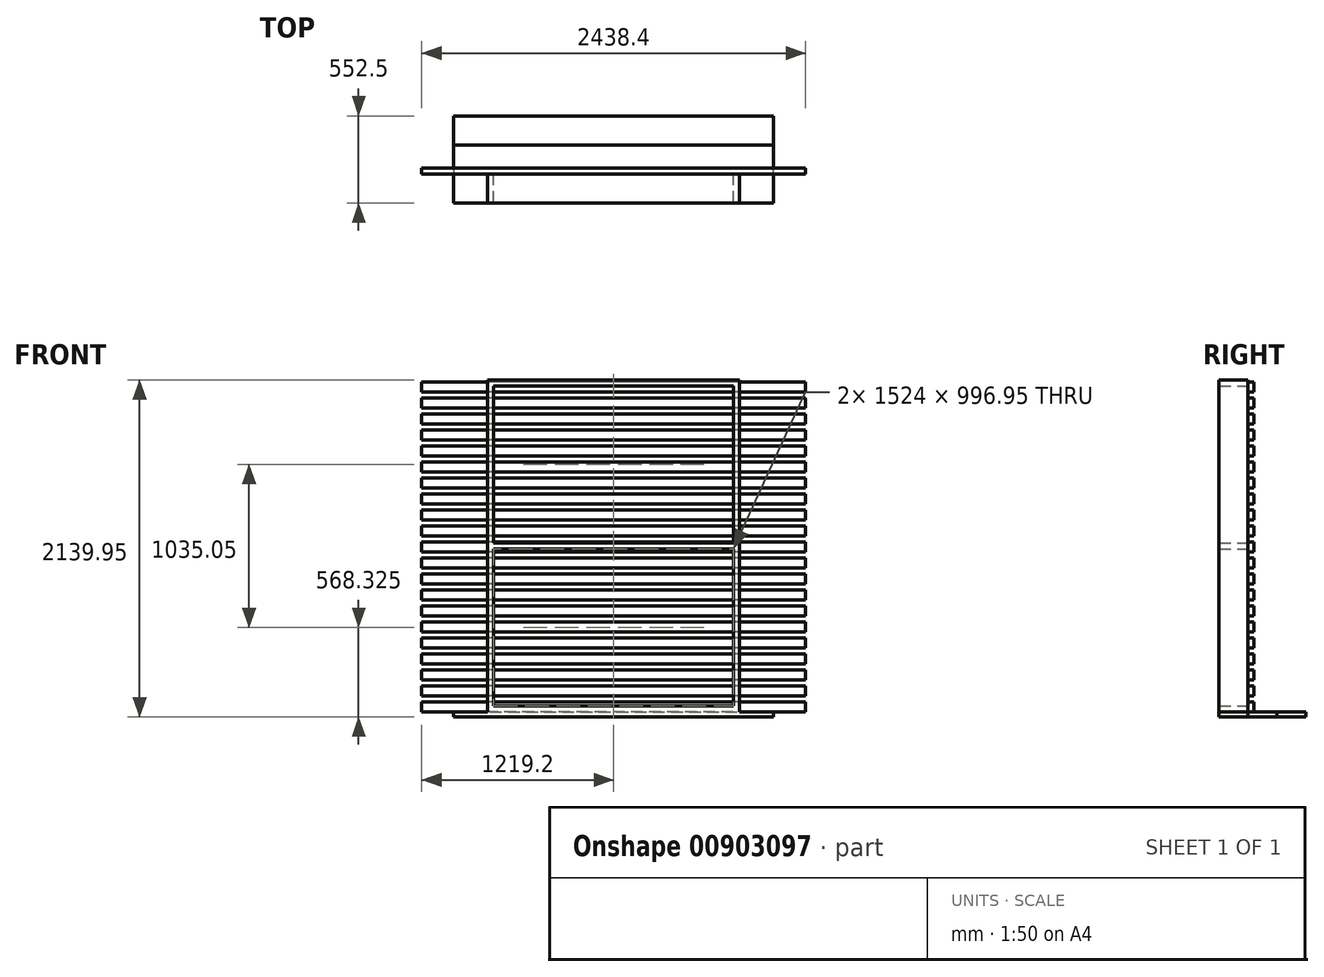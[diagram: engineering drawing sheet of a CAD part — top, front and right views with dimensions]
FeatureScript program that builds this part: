
annotation { "Feature Type Name" : "Feature", "Feature Type Description" : "" }
export const myFeature = defineFeature(function(context is Context, id is Id, definition is map)
    precondition{}
    {
        {
            var Q0;
            Q0=qCreatedBy(makeId("Front.planeOp"),FACE);
            var sketch = newSketch(context, id + "F0", { "sketchPlane" : qUnion([Q0])});
            skLineSegment(sketch, "E0.bottom", {"start": v(762, 1016) * mm, "end": v(-762, 1016) * mm});
            skLineSegment(sketch, "E0.top", {"start": v(762, -1016) * mm, "end": v(-762, -1016) * mm});
            skLineSegment(sketch, "E0.left", {"start": v(762, 1016) * mm, "end": v(762, -1016) * mm});
            skLineSegment(sketch, "E0.right", {"start": v(-762, 1016) * mm, "end": v(-762, -1016) * mm});
            skPoint(sketch, "E0.middle", {"position": v(0, 0) * mm});
            skLineSegment(sketch, "E1.0", {"start": v(800.1, 1054.1) * mm, "end": v(-800.1, 1054.1) * mm});
            skLineSegment(sketch, "E1.1", {"start": v(800.1, 1054.1) * mm, "end": v(800.1, -1054.1) * mm});
            skLineSegment(sketch, "E1.2", {"start": v(800.1, -1054.1) * mm, "end": v(-800.1, -1054.1) * mm});
            skLineSegment(sketch, "E1.3", {"start": v(-800.1, 1054.1) * mm, "end": v(-800.1, -1054.1) * mm});
            skSolve(sketch);
        }
        {
            var Q0;
            Q0=makeQuery(id+"F0.imprint","IMPRINT",FACE,{"disambiguationData":[TD([[makeQuery(id+"F0.imprint","IMPRINT",EDGE,{"derivedFrom":sQuery(id+"F0.wireOp",EDGE,"E0.bottom")}),-1.0]])]});
            extrude(context, id + "F1", {"entities" : qUnion([Q0]), "depth" : 184.15 * mm, "offsetDistance" : 25.4 * mm});
        }
        {
            var Q0;
            Q0=makeQuery(id+"F1.opExtrude","CAP_FACE",FACE,{"disambiguationData":[OSD([sQuery(id+"F0.wireOp",EDGE,"E0.bottom"),sQuery(id+"F0.wireOp",EDGE,"E0.top"),sQuery(id+"F0.wireOp",EDGE,"E0.left"),sQuery(id+"F0.wireOp",EDGE,"E0.right"),sQuery(id+"F0.wireOp",EDGE,"E1.0"),sQuery(id+"F0.wireOp",EDGE,"E1.1"),sQuery(id+"F0.wireOp",EDGE,"E1.2"),sQuery(id+"F0.wireOp",EDGE,"E1.3")])],"isStart":true});
            var sketch = newSketch(context, id + "F2", { "sketchPlane" : qUnion([Q0])});
            skLineSegment(sketch, "E2.bottom", {"start": v(952.5, -92.07) * mm, "end": v(-952.5, -92.08) * mm});
            skLineSegment(sketch, "E2.top", {"start": v(952.5, 92.08) * mm, "end": v(-952.5, 92.07) * mm});
            skLineSegment(sketch, "E2.left", {"start": v(952.5, -92.07) * mm, "end": v(952.5, 92.08) * mm});
            skLineSegment(sketch, "E2.right", {"start": v(-952.5, -92.08) * mm, "end": v(-952.5, 92.07) * mm});
            skPoint(sketch, "E2.middle", {"position": v(0, 0) * mm});
            skLineSegment(sketch, "E3.0.1.0", {"start": v(953.01, 111.12) * mm, "end": v(-951.99, 111.12) * mm});
            skPoint(sketch, "E3.0.1.1", {"position": v(0.51, 203.2) * mm});
            skLineSegment(sketch, "E3.0.1.2", {"start": v(953.01, 111.12) * mm, "end": v(953.01, 295.27) * mm});
            skLineSegment(sketch, "E3.0.1.3", {"start": v(953.01, 295.27) * mm, "end": v(-951.99, 295.27) * mm});
            skLineSegment(sketch, "E3.0.1.4", {"start": v(-951.99, 111.12) * mm, "end": v(-951.99, 295.27) * mm});
            skLineSegment(sketch, "E3.0.2.0", {"start": v(953.53, 314.32) * mm, "end": v(-951.47, 314.32) * mm});
            skPoint(sketch, "E3.0.2.1", {"position": v(1.03, 406.4) * mm});
            skLineSegment(sketch, "E3.0.2.2", {"start": v(953.53, 314.32) * mm, "end": v(953.53, 498.47) * mm});
            skLineSegment(sketch, "E3.0.2.3", {"start": v(953.53, 498.47) * mm, "end": v(-951.47, 498.47) * mm});
            skLineSegment(sketch, "E3.0.2.4", {"start": v(-951.47, 314.32) * mm, "end": v(-951.47, 498.47) * mm});
            skLineSegment(sketch, "E3.0.3.0", {"start": v(954.04, 517.52) * mm, "end": v(-950.96, 517.52) * mm});
            skPoint(sketch, "E3.0.3.1", {"position": v(1.54, 609.6) * mm});
            skLineSegment(sketch, "E3.0.3.2", {"start": v(954.04, 517.52) * mm, "end": v(954.04, 701.67) * mm});
            skLineSegment(sketch, "E3.0.3.3", {"start": v(954.04, 701.67) * mm, "end": v(-950.96, 701.67) * mm});
            skLineSegment(sketch, "E3.0.3.4", {"start": v(-950.96, 517.52) * mm, "end": v(-950.96, 701.67) * mm});
            skLineSegment(sketch, "E3.0.4.0", {"start": v(954.56, 720.72) * mm, "end": v(-950.44, 720.72) * mm});
            skPoint(sketch, "E3.0.4.1", {"position": v(2.06, 812.8) * mm});
            skLineSegment(sketch, "E3.0.4.2", {"start": v(954.56, 720.72) * mm, "end": v(954.56, 904.87) * mm});
            skLineSegment(sketch, "E3.0.4.3", {"start": v(954.56, 904.87) * mm, "end": v(-950.44, 904.87) * mm});
            skLineSegment(sketch, "E3.0.4.4", {"start": v(-950.44, 720.72) * mm, "end": v(-950.44, 904.87) * mm});
            skLineSegment(sketch, "E3.0.5.0", {"start": v(955.07, 923.92) * mm, "end": v(-949.93, 923.92) * mm});
            skPoint(sketch, "E3.0.5.1", {"position": v(2.57, 1016) * mm});
            skLineSegment(sketch, "E3.0.5.2", {"start": v(955.07, 923.92) * mm, "end": v(955.07, 1108.07) * mm});
            skLineSegment(sketch, "E3.0.5.3", {"start": v(955.07, 1108.07) * mm, "end": v(-949.93, 1108.07) * mm});
            skLineSegment(sketch, "E3.0.5.4", {"start": v(-949.93, 923.92) * mm, "end": v(-949.93, 1108.07) * mm});
            skLineSegment(sketch, "E3.direction1", {"start": v(-952.5, -92.08) * mm, "end": v(-952.5, -92.08) * mm});
            skLineSegment(sketch, "E3.direction2", {"start": v(-952.5, -92.08) * mm, "end": v(-951.99, 111.12) * mm, "construction": true});
            skLineSegment(sketch, "E4", {"start": v(0, 0) * mm, "end": v(1562.61, 0) * mm});
            skLineSegment(sketch, "E5.MirrorCS", {"start": v(954.56, -720.72) * mm, "end": v(-950.44, -720.72) * mm});
            skPoint(sketch, "E6.MirrorP", {"position": v(1.03, -406.4) * mm});
            skLineSegment(sketch, "E7.MirrorCS", {"start": v(953.01, -111.12) * mm, "end": v(-951.99, -111.12) * mm});
            skLineSegment(sketch, "E8.MirrorCS", {"start": v(-949.93, -923.92) * mm, "end": v(-949.93, -1108.07) * mm});
            skLineSegment(sketch, "E9.MirrorCS", {"start": v(954.04, -517.52) * mm, "end": v(-950.96, -517.52) * mm});
            skLineSegment(sketch, "E10.MirrorCS", {"start": v(953.53, -314.32) * mm, "end": v(953.53, -498.47) * mm});
            skLineSegment(sketch, "E11.MirrorCS", {"start": v(953.01, -111.12) * mm, "end": v(953.01, -295.27) * mm});
            skPoint(sketch, "E12.MirrorP", {"position": v(2.06, -812.8) * mm});
            skLineSegment(sketch, "E13.MirrorCS", {"start": v(-950.96, -517.52) * mm, "end": v(-950.96, -701.67) * mm});
            skLineSegment(sketch, "E14.MirrorCS", {"start": v(953.53, -498.47) * mm, "end": v(-951.47, -498.47) * mm});
            skLineSegment(sketch, "E15.MirrorCS", {"start": v(954.04, -517.52) * mm, "end": v(954.04, -701.67) * mm});
            skLineSegment(sketch, "E16.MirrorCS", {"start": v(955.07, -923.92) * mm, "end": v(-949.93, -923.92) * mm});
            skLineSegment(sketch, "E17.MirrorCS", {"start": v(954.56, -720.72) * mm, "end": v(954.56, -904.87) * mm});
            skLineSegment(sketch, "E18.MirrorCS", {"start": v(955.07, -923.92) * mm, "end": v(955.07, -1108.07) * mm});
            skPoint(sketch, "E19.MirrorP", {"position": v(1.54, -609.6) * mm});
            skLineSegment(sketch, "E20.MirrorCS", {"start": v(-951.99, -111.12) * mm, "end": v(-951.99, -295.27) * mm});
            skLineSegment(sketch, "E21.MirrorCS", {"start": v(954.04, -701.67) * mm, "end": v(-950.96, -701.67) * mm});
            skPoint(sketch, "E22.MirrorP", {"position": v(0.51, -203.2) * mm});
            skLineSegment(sketch, "E23.MirrorCS", {"start": v(953.53, -314.32) * mm, "end": v(-951.47, -314.32) * mm});
            skLineSegment(sketch, "E24.MirrorCS", {"start": v(955.07, -1108.07) * mm, "end": v(-949.93, -1108.07) * mm});
            skLineSegment(sketch, "E25.MirrorCS", {"start": v(953.01, -295.27) * mm, "end": v(-951.99, -295.27) * mm});
            skLineSegment(sketch, "E26.MirrorCS", {"start": v(-951.47, -314.32) * mm, "end": v(-951.47, -498.47) * mm});
            skPoint(sketch, "E27.MirrorP", {"position": v(2.57, -1016) * mm});
            skLineSegment(sketch, "E28.MirrorCS", {"start": v(-950.44, -720.72) * mm, "end": v(-950.44, -904.87) * mm});
            skLineSegment(sketch, "E29.MirrorCS", {"start": v(954.56, -904.87) * mm, "end": v(-950.44, -904.87) * mm});
            skSolve(sketch);
        }
        {
            var Q0;
            Q0=qCreatedBy(makeId("Top.planeOp"),FACE);
            var sketch = newSketch(context, id + "F3", { "sketchPlane" : qUnion([Q0])});
            skLineSegment(sketch, "E30.0", {"start": v(-762, -184.15) * mm, "end": v(-762, 0) * mm});
            skLineSegment(sketch, "E31.0", {"start": v(762, -184.15) * mm, "end": v(762, 0) * mm});
            skLineSegment(sketch, "E32", {"start": v(-762, 0) * mm, "end": v(762, 0) * mm});
            skLineSegment(sketch, "E33", {"start": v(-762, -184.15) * mm, "end": v(762, -184.15) * mm});
            skSolve(sketch);
        }
        {
            var Q0;
            Q0 = qSketchRegion(id + "F3", true);
            extrude(context, id + "F4", {"entities" : qUnion([Q0]), "operationType" : NewBodyOperationType.ADD, "endBound" : BoundingType.SYMMETRIC, "depth" : 38.1 * mm, "offsetDistance" : 25.4 * mm});
        }
        {
            var Q0;
            Q0=makeQuery(id+"F1.opExtrude","SWEPT_FACE",FACE,{"disambiguationData":[OSD([sQuery(id+"F0.wireOp",EDGE,"E1.2")])]});
            var sketch = newSketch(context, id + "F5", { "sketchPlane" : qUnion([Q0])});
            skLineSegment(sketch, "E34", {"start": v(0, 0) * mm, "end": v(-1016, 0) * mm});
            skLineSegment(sketch, "E35", {"start": v(0, 0) * mm, "end": v(1016, 0) * mm});
            skLineSegment(sketch, "E36", {"start": v(-1016, 0) * mm, "end": v(-1016, 184.15) * mm});
            skLineSegment(sketch, "E37", {"start": v(-1016, 184.15) * mm, "end": v(1016, 184.15) * mm});
            skLineSegment(sketch, "E38", {"start": v(1016, 184.15) * mm, "end": v(1016, 0) * mm});
            skLineSegment(sketch, "E39.0.1.0", {"start": v(-1016, -0.03) * mm, "end": v(1016, -0.03) * mm});
            skLineSegment(sketch, "E39.0.1.1", {"start": v(1016, -0.03) * mm, "end": v(1016, -184.18) * mm});
            skLineSegment(sketch, "E39.0.1.2", {"start": v(0, -184.18) * mm, "end": v(1016, -184.18) * mm});
            skLineSegment(sketch, "E39.0.1.3", {"start": v(-1016, -184.18) * mm, "end": v(-1016, -0.03) * mm});
            skLineSegment(sketch, "E39.0.1.4", {"start": v(0, -184.18) * mm, "end": v(-1016, -184.18) * mm});
            skLineSegment(sketch, "E39.0.2.0", {"start": v(-1016, -184.2) * mm, "end": v(1016, -184.2) * mm});
            skLineSegment(sketch, "E39.0.2.1", {"start": v(1016, -184.2) * mm, "end": v(1016, -368.35) * mm});
            skLineSegment(sketch, "E39.0.2.2", {"start": v(0, -368.35) * mm, "end": v(1016, -368.35) * mm});
            skLineSegment(sketch, "E39.0.2.3", {"start": v(-1016, -368.35) * mm, "end": v(-1016, -184.2) * mm});
            skLineSegment(sketch, "E39.0.2.4", {"start": v(0, -368.35) * mm, "end": v(-1016, -368.35) * mm});
            skLineSegment(sketch, "E39.1.1.0", {"start": v(-1016, -0.03) * mm, "end": v(1016, -0.03) * mm});
            skLineSegment(sketch, "E39.1.1.1", {"start": v(1016, -0.03) * mm, "end": v(1016, -184.18) * mm});
            skLineSegment(sketch, "E39.1.1.2", {"start": v(0, -184.18) * mm, "end": v(1016, -184.18) * mm});
            skLineSegment(sketch, "E39.1.1.3", {"start": v(-1016, -184.18) * mm, "end": v(-1016, -0.03) * mm});
            skLineSegment(sketch, "E39.1.1.4", {"start": v(0, -184.18) * mm, "end": v(-1016, -184.18) * mm});
            skLineSegment(sketch, "E39.1.2.0", {"start": v(-1016, -184.2) * mm, "end": v(1016, -184.2) * mm});
            skLineSegment(sketch, "E39.1.2.1", {"start": v(1016, -184.2) * mm, "end": v(1016, -368.35) * mm});
            skLineSegment(sketch, "E39.1.2.2", {"start": v(0, -368.35) * mm, "end": v(1016, -368.35) * mm});
            skLineSegment(sketch, "E39.1.2.3", {"start": v(-1016, -368.35) * mm, "end": v(-1016, -184.2) * mm});
            skLineSegment(sketch, "E39.1.2.4", {"start": v(0, -368.35) * mm, "end": v(-1016, -368.35) * mm});
            skLineSegment(sketch, "E39.2.1.0", {"start": v(-1016, -0.03) * mm, "end": v(1016, -0.03) * mm});
            skLineSegment(sketch, "E39.2.1.1", {"start": v(1016, -0.03) * mm, "end": v(1016, -184.18) * mm});
            skLineSegment(sketch, "E39.2.1.2", {"start": v(0, -184.18) * mm, "end": v(1016, -184.18) * mm});
            skLineSegment(sketch, "E39.2.1.3", {"start": v(-1016, -184.18) * mm, "end": v(-1016, -0.03) * mm});
            skLineSegment(sketch, "E39.2.1.4", {"start": v(0, -184.18) * mm, "end": v(-1016, -184.18) * mm});
            skLineSegment(sketch, "E39.2.2.0", {"start": v(-1016, -184.2) * mm, "end": v(1016, -184.2) * mm});
            skLineSegment(sketch, "E39.2.2.1", {"start": v(1016, -184.2) * mm, "end": v(1016, -368.35) * mm});
            skLineSegment(sketch, "E39.2.2.2", {"start": v(0, -368.35) * mm, "end": v(1016, -368.35) * mm});
            skLineSegment(sketch, "E39.2.2.3", {"start": v(-1016, -368.35) * mm, "end": v(-1016, -184.2) * mm});
            skLineSegment(sketch, "E39.2.2.4", {"start": v(0, -368.35) * mm, "end": v(-1016, -368.35) * mm});
            skLineSegment(sketch, "E39.direction1", {"start": v(-1016, 0) * mm, "end": v(-1016, 0) * mm});
            skLineSegment(sketch, "E39.direction2", {"start": v(-1016, 0) * mm, "end": v(-1016, -184.18) * mm, "construction": true});
            skSolve(sketch);
        }
        {
            var Q0;
            Q0 = qSketchRegion(id + "F5", true);
            extrude(context, id + "F6", {"entities" : qUnion([Q0]), "operationType" : NewBodyOperationType.ADD, "depth" : 31.75 * mm, "offsetDistance" : 25.4 * mm});
        }
        {
            var Q0;
            Q0=qCreatedBy(makeId("Right.planeOp"),FACE);
            var sketch = newSketch(context, id + "F7", { "sketchPlane" : qUnion([Q0])});
            skLineSegment(sketch, "E40.bottom", {"start": v(0, -1054.1) * mm, "end": v(38.1, -1054.1) * mm});
            skLineSegment(sketch, "E40.top", {"start": v(0, -990.6) * mm, "end": v(38.1, -990.6) * mm});
            skLineSegment(sketch, "E40.left", {"start": v(0, -1054.1) * mm, "end": v(0, -990.6) * mm});
            skLineSegment(sketch, "E40.right", {"start": v(38.1, -1054.1) * mm, "end": v(38.1, -990.6) * mm});
            skLineSegment(sketch, "E41.0.1.0", {"start": v(0, -952.5) * mm, "end": v(0, -889) * mm});
            skLineSegment(sketch, "E41.0.1.1", {"start": v(38.1, -952.5) * mm, "end": v(38.1, -889) * mm});
            skLineSegment(sketch, "E41.0.1.2", {"start": v(0, -952.5) * mm, "end": v(38.1, -952.5) * mm});
            skLineSegment(sketch, "E41.0.1.3", {"start": v(0, -889) * mm, "end": v(38.1, -889) * mm});
            skLineSegment(sketch, "E41.0.2.0", {"start": v(0, -850.9) * mm, "end": v(0, -787.4) * mm});
            skLineSegment(sketch, "E41.0.2.1", {"start": v(38.1, -850.9) * mm, "end": v(38.1, -787.4) * mm});
            skLineSegment(sketch, "E41.0.2.2", {"start": v(0, -850.9) * mm, "end": v(38.1, -850.9) * mm});
            skLineSegment(sketch, "E41.0.2.3", {"start": v(0, -787.4) * mm, "end": v(38.1, -787.4) * mm});
            skLineSegment(sketch, "E41.0.3.0", {"start": v(0, -749.3) * mm, "end": v(0, -685.8) * mm});
            skLineSegment(sketch, "E41.0.3.1", {"start": v(38.1, -749.3) * mm, "end": v(38.1, -685.8) * mm});
            skLineSegment(sketch, "E41.0.3.2", {"start": v(0, -749.3) * mm, "end": v(38.1, -749.3) * mm});
            skLineSegment(sketch, "E41.0.3.3", {"start": v(0, -685.8) * mm, "end": v(38.1, -685.8) * mm});
            skLineSegment(sketch, "E41.0.4.0", {"start": v(0, -647.7) * mm, "end": v(0, -584.2) * mm});
            skLineSegment(sketch, "E41.0.4.1", {"start": v(38.1, -647.7) * mm, "end": v(38.1, -584.2) * mm});
            skLineSegment(sketch, "E41.0.4.2", {"start": v(0, -647.7) * mm, "end": v(38.1, -647.7) * mm});
            skLineSegment(sketch, "E41.0.4.3", {"start": v(0, -584.2) * mm, "end": v(38.1, -584.2) * mm});
            skLineSegment(sketch, "E41.0.5.0", {"start": v(0, -546.1) * mm, "end": v(0, -482.6) * mm});
            skLineSegment(sketch, "E41.0.5.1", {"start": v(38.1, -546.1) * mm, "end": v(38.1, -482.6) * mm});
            skLineSegment(sketch, "E41.0.5.2", {"start": v(0, -546.1) * mm, "end": v(38.1, -546.1) * mm});
            skLineSegment(sketch, "E41.0.5.3", {"start": v(0, -482.6) * mm, "end": v(38.1, -482.6) * mm});
            skLineSegment(sketch, "E41.0.6.0", {"start": v(0, -444.5) * mm, "end": v(0, -381) * mm});
            skLineSegment(sketch, "E41.0.6.1", {"start": v(38.1, -444.5) * mm, "end": v(38.1, -381) * mm});
            skLineSegment(sketch, "E41.0.6.2", {"start": v(0, -444.5) * mm, "end": v(38.1, -444.5) * mm});
            skLineSegment(sketch, "E41.0.6.3", {"start": v(0, -381) * mm, "end": v(38.1, -381) * mm});
            skLineSegment(sketch, "E41.0.7.0", {"start": v(0, -342.9) * mm, "end": v(0, -279.4) * mm});
            skLineSegment(sketch, "E41.0.7.1", {"start": v(38.1, -342.9) * mm, "end": v(38.1, -279.4) * mm});
            skLineSegment(sketch, "E41.0.7.2", {"start": v(0, -342.9) * mm, "end": v(38.1, -342.9) * mm});
            skLineSegment(sketch, "E41.0.7.3", {"start": v(0, -279.4) * mm, "end": v(38.1, -279.4) * mm});
            skLineSegment(sketch, "E41.0.8.0", {"start": v(0, -241.3) * mm, "end": v(0, -177.8) * mm});
            skLineSegment(sketch, "E41.0.8.1", {"start": v(38.1, -241.3) * mm, "end": v(38.1, -177.8) * mm});
            skLineSegment(sketch, "E41.0.8.2", {"start": v(0, -241.3) * mm, "end": v(38.1, -241.3) * mm});
            skLineSegment(sketch, "E41.0.8.3", {"start": v(0, -177.8) * mm, "end": v(38.1, -177.8) * mm});
            skLineSegment(sketch, "E41.0.9.0", {"start": v(0, -139.7) * mm, "end": v(0, -76.2) * mm});
            skLineSegment(sketch, "E41.0.9.1", {"start": v(38.1, -139.7) * mm, "end": v(38.1, -76.2) * mm});
            skLineSegment(sketch, "E41.0.9.2", {"start": v(0, -139.7) * mm, "end": v(38.1, -139.7) * mm});
            skLineSegment(sketch, "E41.0.9.3", {"start": v(0, -76.2) * mm, "end": v(38.1, -76.2) * mm});
            skLineSegment(sketch, "E41.0.10.0", {"start": v(0, -38.1) * mm, "end": v(0, 25.4) * mm});
            skLineSegment(sketch, "E41.0.10.1", {"start": v(38.1, -38.1) * mm, "end": v(38.1, 25.4) * mm});
            skLineSegment(sketch, "E41.0.10.2", {"start": v(0, -38.1) * mm, "end": v(38.1, -38.1) * mm});
            skLineSegment(sketch, "E41.0.10.3", {"start": v(0, 25.4) * mm, "end": v(38.1, 25.4) * mm});
            skLineSegment(sketch, "E41.direction1", {"start": v(0, -1054.1) * mm, "end": v(25.4, -1054.1) * mm, "construction": true});
            skLineSegment(sketch, "E41.direction2", {"start": v(0, -1054.1) * mm, "end": v(0, -952.5) * mm, "construction": true});
            skLineSegment(sketch, "E42.0.0.11", {"start": v(0, 63.5) * mm, "end": v(0, 127) * mm});
            skLineSegment(sketch, "E42.3.0.11", {"start": v(38.1, 63.5) * mm, "end": v(38.1, 127) * mm});
            skLineSegment(sketch, "E42.6.0.11", {"start": v(0, 63.5) * mm, "end": v(38.1, 63.5) * mm});
            skLineSegment(sketch, "E42.9.0.11", {"start": v(0, 127) * mm, "end": v(38.1, 127) * mm});
            skLineSegment(sketch, "E42.0.0.12", {"start": v(0, 165.1) * mm, "end": v(0, 228.6) * mm});
            skLineSegment(sketch, "E42.3.0.12", {"start": v(38.1, 165.1) * mm, "end": v(38.1, 228.6) * mm});
            skLineSegment(sketch, "E42.6.0.12", {"start": v(0, 165.1) * mm, "end": v(38.1, 165.1) * mm});
            skLineSegment(sketch, "E42.9.0.12", {"start": v(0, 228.6) * mm, "end": v(38.1, 228.6) * mm});
            skLineSegment(sketch, "E42.0.0.13", {"start": v(0, 266.7) * mm, "end": v(0, 330.2) * mm});
            skLineSegment(sketch, "E42.3.0.13", {"start": v(38.1, 266.7) * mm, "end": v(38.1, 330.2) * mm});
            skLineSegment(sketch, "E42.6.0.13", {"start": v(0, 266.7) * mm, "end": v(38.1, 266.7) * mm});
            skLineSegment(sketch, "E42.9.0.13", {"start": v(0, 330.2) * mm, "end": v(38.1, 330.2) * mm});
            skLineSegment(sketch, "E42.0.0.14", {"start": v(0, 368.3) * mm, "end": v(0, 431.8) * mm});
            skLineSegment(sketch, "E42.3.0.14", {"start": v(38.1, 368.3) * mm, "end": v(38.1, 431.8) * mm});
            skLineSegment(sketch, "E42.6.0.14", {"start": v(0, 368.3) * mm, "end": v(38.1, 368.3) * mm});
            skLineSegment(sketch, "E42.9.0.14", {"start": v(0, 431.8) * mm, "end": v(38.1, 431.8) * mm});
            skLineSegment(sketch, "E42.0.0.15", {"start": v(0, 469.9) * mm, "end": v(0, 533.4) * mm});
            skLineSegment(sketch, "E42.3.0.15", {"start": v(38.1, 469.9) * mm, "end": v(38.1, 533.4) * mm});
            skLineSegment(sketch, "E42.6.0.15", {"start": v(0, 469.9) * mm, "end": v(38.1, 469.9) * mm});
            skLineSegment(sketch, "E42.9.0.15", {"start": v(0, 533.4) * mm, "end": v(38.1, 533.4) * mm});
            skLineSegment(sketch, "E42.0.0.16", {"start": v(0, 571.5) * mm, "end": v(0, 635) * mm});
            skLineSegment(sketch, "E42.3.0.16", {"start": v(38.1, 571.5) * mm, "end": v(38.1, 635) * mm});
            skLineSegment(sketch, "E42.6.0.16", {"start": v(0, 571.5) * mm, "end": v(38.1, 571.5) * mm});
            skLineSegment(sketch, "E42.9.0.16", {"start": v(0, 635) * mm, "end": v(38.1, 635) * mm});
            skLineSegment(sketch, "E42.0.0.17", {"start": v(0, 673.1) * mm, "end": v(0, 736.6) * mm});
            skLineSegment(sketch, "E42.3.0.17", {"start": v(38.1, 673.1) * mm, "end": v(38.1, 736.6) * mm});
            skLineSegment(sketch, "E42.6.0.17", {"start": v(0, 673.1) * mm, "end": v(38.1, 673.1) * mm});
            skLineSegment(sketch, "E42.9.0.17", {"start": v(0, 736.6) * mm, "end": v(38.1, 736.6) * mm});
            skLineSegment(sketch, "E42.0.0.18", {"start": v(0, 774.7) * mm, "end": v(0, 838.2) * mm});
            skLineSegment(sketch, "E42.3.0.18", {"start": v(38.1, 774.7) * mm, "end": v(38.1, 838.2) * mm});
            skLineSegment(sketch, "E42.6.0.18", {"start": v(0, 774.7) * mm, "end": v(38.1, 774.7) * mm});
            skLineSegment(sketch, "E42.9.0.18", {"start": v(0, 838.2) * mm, "end": v(38.1, 838.2) * mm});
            skLineSegment(sketch, "E43.0.0.19", {"start": v(0, 876.3) * mm, "end": v(0, 939.8) * mm});
            skLineSegment(sketch, "E43.3.0.19", {"start": v(38.1, 876.3) * mm, "end": v(38.1, 939.8) * mm});
            skLineSegment(sketch, "E43.6.0.19", {"start": v(0, 876.3) * mm, "end": v(38.1, 876.3) * mm});
            skLineSegment(sketch, "E43.9.0.19", {"start": v(0, 939.8) * mm, "end": v(38.1, 939.8) * mm});
            skLineSegment(sketch, "E43.0.0.20", {"start": v(0, 977.9) * mm, "end": v(0, 1041.4) * mm});
            skLineSegment(sketch, "E43.3.0.20", {"start": v(38.1, 977.9) * mm, "end": v(38.1, 1041.4) * mm});
            skLineSegment(sketch, "E43.6.0.20", {"start": v(0, 977.9) * mm, "end": v(38.1, 977.9) * mm});
            skLineSegment(sketch, "E43.9.0.20", {"start": v(0, 1041.4) * mm, "end": v(38.1, 1041.4) * mm});
            skSolve(sketch);
        }
        {
            var Q0;
            Q0 = qSketchRegion(id + "F7", true);
            extrude(context, id + "F8", {"entities" : qUnion([Q0]), "endBound" : BoundingType.SYMMETRIC, "depth" : 2438.4 * mm, "offsetDistance" : 25.4 * mm});
        }
    });
